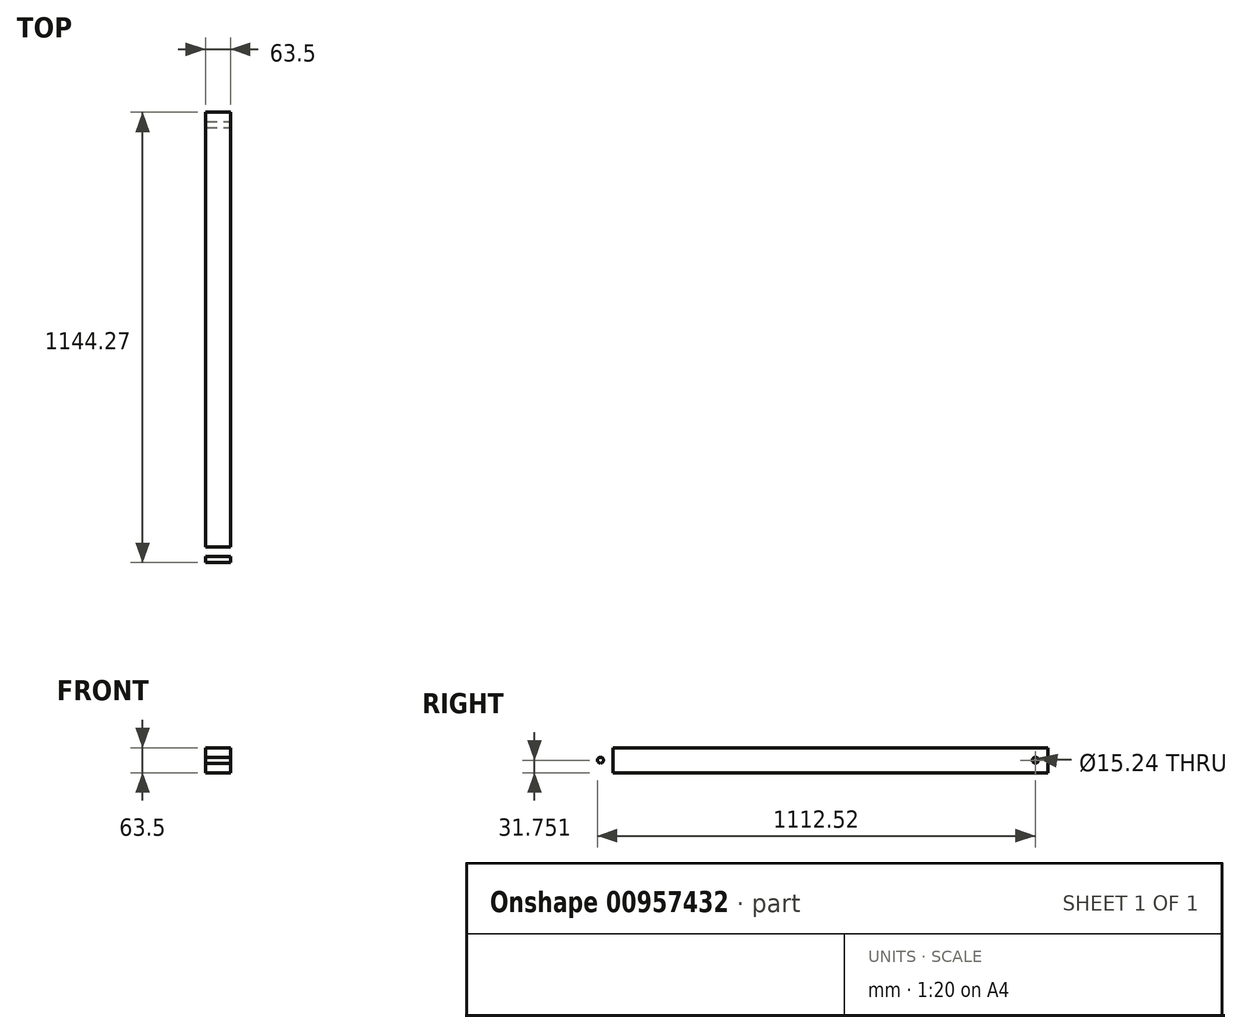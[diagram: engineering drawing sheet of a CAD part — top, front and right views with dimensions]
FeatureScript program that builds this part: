
annotation { "Feature Type Name" : "Feature", "Feature Type Description" : "" }
export const myFeature = defineFeature(function(context is Context, id is Id, definition is map)
    precondition{}
    {
        {
            var Q0;
            Q0=qCreatedBy(makeId("Front.planeOp"),FACE);
            var sketch = newSketch(context, id + "F0", { "sketchPlane" : qUnion([Q0])});
            skLineSegment(sketch, "E0.bottom", {"start": v(-96.97, 96.54) * mm, "end": v(-33.47, 96.54) * mm});
            skLineSegment(sketch, "E0.top", {"start": v(-96.97, 33.04) * mm, "end": v(-33.47, 33.04) * mm});
            skLineSegment(sketch, "E0.left", {"start": v(-96.97, 96.54) * mm, "end": v(-96.97, 33.04) * mm});
            skLineSegment(sketch, "E0.right", {"start": v(-33.47, 96.54) * mm, "end": v(-33.47, 33.04) * mm});
            skSolve(sketch);
        }
        {
            var Q0;
            Q0=makeQuery(id+"F0.imprint","IMPRINT",FACE,{"disambiguationData":[TD([[makeQuery(id+"F0.imprint","IMPRINT",EDGE,{"derivedFrom":sQuery(id+"F0.wireOp",EDGE,"E0.bottom")}),-1.0]])]});
            extrude(context, id + "F1", {"entities" : qUnion([Q0]), "oppositeDirection" : true, "depth" : 1168.4 * mm, "offsetDistance" : 25.4 * mm});
        }
        {
            var Q0;
            Q0=makeQuery(id+"F1.opExtrude","SWEPT_FACE",FACE,{"disambiguationData":[OSD([sQuery(id+"F0.wireOp",EDGE,"E0.left")])]});
            var sketch = newSketch(context, id + "F2", { "sketchPlane" : qUnion([Q0])});
            skLineSegment(sketch, "E1.bottom", {"start": v(-1168.4, 33.04) * mm, "end": v(-1104.9, 33.04) * mm});
            skLineSegment(sketch, "E1.top", {"start": v(-1168.4, 96.54) * mm, "end": v(-1104.9, 96.54) * mm});
            skLineSegment(sketch, "E1.left", {"start": v(-1168.4, 33.04) * mm, "end": v(-1168.4, 96.54) * mm});
            skLineSegment(sketch, "E1.right", {"start": v(-1104.9, 33.04) * mm, "end": v(-1104.9, 96.54) * mm});
            skLineSegment(sketch, "E2", {"start": v(-1168.4, 96.54) * mm, "end": v(-1136.65, 96.54) * mm});
            skLineSegment(sketch, "E3", {"start": v(-1136.65, 96.54) * mm, "end": v(-1136.65, 33.04) * mm});
            skCircle(sketch, "E4", {"center": v(-1136.65, 64.8) * mm, "radius": 7.62 * mm});
            skSolve(sketch);
        }
        {
            var Q0;
            Q0 = qSketchRegion(id + "F2", true);
            extrude(context, id + "F3", {"entities" : qUnion([Q0]), "operationType" : NewBodyOperationType.ADD, "depth" : 25.4 * mm, "offsetDistance" : 25.4 * mm});
        }
        {
            var Q0;
            Q0=makeQuery(id+"F3.boolean.opBoolean","SPLIT",FACE,{"disambiguationData":[TD([makeQuery(id+"F3.opExtrude","SWEPT_FACE",FACE,{"disambiguationData":[OSD([sQuery(id+"F2.wireOp",EDGE,"E4")])]})])],"derivedFrom":makeQuery(id+"F1.opExtrude","SWEPT_FACE",FACE,{"disambiguationData":[OSD([sQuery(id+"F0.wireOp",EDGE,"E0.left")])]})});
            extrude(context, id + "F4", {"entities" : qUnion([Q0]), "operationType" : NewBodyOperationType.REMOVE, "oppositeDirection" : true, "depth" : 63.5 * mm, "offsetDistance" : 25.4 * mm});
        }
        {
            var Q0;
            Q0=makeQuery(id+"F3.boolean.opBoolean","MERGE",FACE,{"derivedFrom":[makeQuery(id+"F1.opExtrude","SWEPT_FACE",FACE,{"disambiguationData":[OSD([sQuery(id+"F0.wireOp",EDGE,"E0.bottom")])]}),makeQuery(id+"F3.opExtrude","SWEPT_FACE",FACE,{"disambiguationData":[OSD([sQuery(id+"F2.wireOp",EDGE,"E1.top"),sQuery(id+"F2.wireOp",EDGE,"E2")])]})]});
            var sketch = newSketch(context, id + "F5", { "sketchPlane" : qUnion([Q0])});
            skLineSegment(sketch, "E5.bottom", {"start": v(-122.37, 1168.4) * mm, "end": v(-96.97, 1168.4) * mm});
            skLineSegment(sketch, "E5.top", {"start": v(-122.37, 1104.9) * mm, "end": v(-96.97, 1104.9) * mm});
            skLineSegment(sketch, "E5.left", {"start": v(-122.37, 1168.4) * mm, "end": v(-122.37, 1104.9) * mm});
            skLineSegment(sketch, "E5.right", {"start": v(-96.97, 1168.4) * mm, "end": v(-96.97, 1104.9) * mm});
            skSolve(sketch);
        }
        {
            var Q0;
            Q0 = qSketchRegion(id + "F5", true);
            extrude(context, id + "F6", {"entities" : qUnion([Q0]), "operationType" : NewBodyOperationType.REMOVE, "oppositeDirection" : true, "depth" : 63.5 * mm, "offsetDistance" : 25.4 * mm});
        }
        {
            var Q0;
            {var subQ0=sQuery(id+"F0.wireOp",EDGE,"E0.left");var subQ2=sQuery(id+"F0.wireOp",EDGE,"E0.bottom");Q0=makeQuery(id+"F6.boolean.opBoolean","MERGE",FACE,{"derivedFrom":[makeQuery(id+"F3.boolean.opBoolean","SPLIT",FACE,{"disambiguationData":[TD([makeQuery(id+"F1.opExtrude","SWEPT_FACE",FACE,{"disambiguationData":[OSD([subQ2])]})])],"derivedFrom":makeQuery(id+"F1.opExtrude","SWEPT_FACE",FACE,{"disambiguationData":[OSD([subQ0])]})})],"fromTools":[makeQuery(id+"F6.opExtrude","SWEPT_FACE",FACE,{"disambiguationData":[OSD([sQuery(id+"F5.wireOp",EDGE,"E5.right")])]})]});}
            var sketch = newSketch(context, id + "F7", { "sketchPlane" : qUnion([Q0])});
            skLineSegment(sketch, "E6.bottom", {"start": v(0, 96.54) * mm, "end": v(-63.5, 96.54) * mm});
            skLineSegment(sketch, "E6.top", {"start": v(0, 33.04) * mm, "end": v(-63.5, 33.04) * mm});
            skLineSegment(sketch, "E6.left", {"start": v(0, 96.54) * mm, "end": v(0, 33.04) * mm});
            skLineSegment(sketch, "E6.right", {"start": v(-63.5, 96.54) * mm, "end": v(-63.5, 33.04) * mm});
            skLineSegment(sketch, "E7", {"start": v(0, 96.54) * mm, "end": v(-31.75, 96.54) * mm});
            skLineSegment(sketch, "E8", {"start": v(-31.75, 96.54) * mm, "end": v(-31.75, 33.04) * mm});
            skCircle(sketch, "E9", {"center": v(-31.75, 64.8) * mm, "radius": 7.62 * mm});
            skSolve(sketch);
        }
        {
            var Q0;
            {var subQ0=sQuery(id+"F7.wireOp",EDGE,"E9");var subQ1=sQuery(id+"F7.wireOp",EDGE,"E8");var subQ2=makeQuery(id+"F7.imprint","INTERSECT",VERTEX,{"disambiguationData":[OD(0.0)],"derivedFrom":[subQ1,subQ0]});Q0=makeQuery(id+"F7.imprint","IMPRINT",FACE,{"disambiguationData":[TD([[makeQuery(id+"F7.imprint","IMPRINT",EDGE,{"disambiguationData":[TD([[subQ2,-1.0]])],"derivedFrom":subQ1}),1.0]])]});}
            var Q1;
            {var subQ0=sQuery(id+"F7.wireOp",EDGE,"E9");var subQ1=sQuery(id+"F7.wireOp",EDGE,"E8");var subQ2=makeQuery(id+"F7.imprint","INTERSECT",VERTEX,{"disambiguationData":[OD(0.0)],"derivedFrom":[subQ1,subQ0]});Q1=makeQuery(id+"F7.imprint","IMPRINT",FACE,{"disambiguationData":[TD([[makeQuery(id+"F7.imprint","IMPRINT",EDGE,{"disambiguationData":[TD([[subQ2,-1.0]])],"derivedFrom":subQ1}),-1.0]])]});}
            extrude(context, id + "F8", {"entities" : qUnion([Q0, Q1]), "operationType" : NewBodyOperationType.REMOVE, "oppositeDirection" : true, "depth" : 76.2 * mm, "offsetDistance" : 25.4 * mm});
        }
    });
